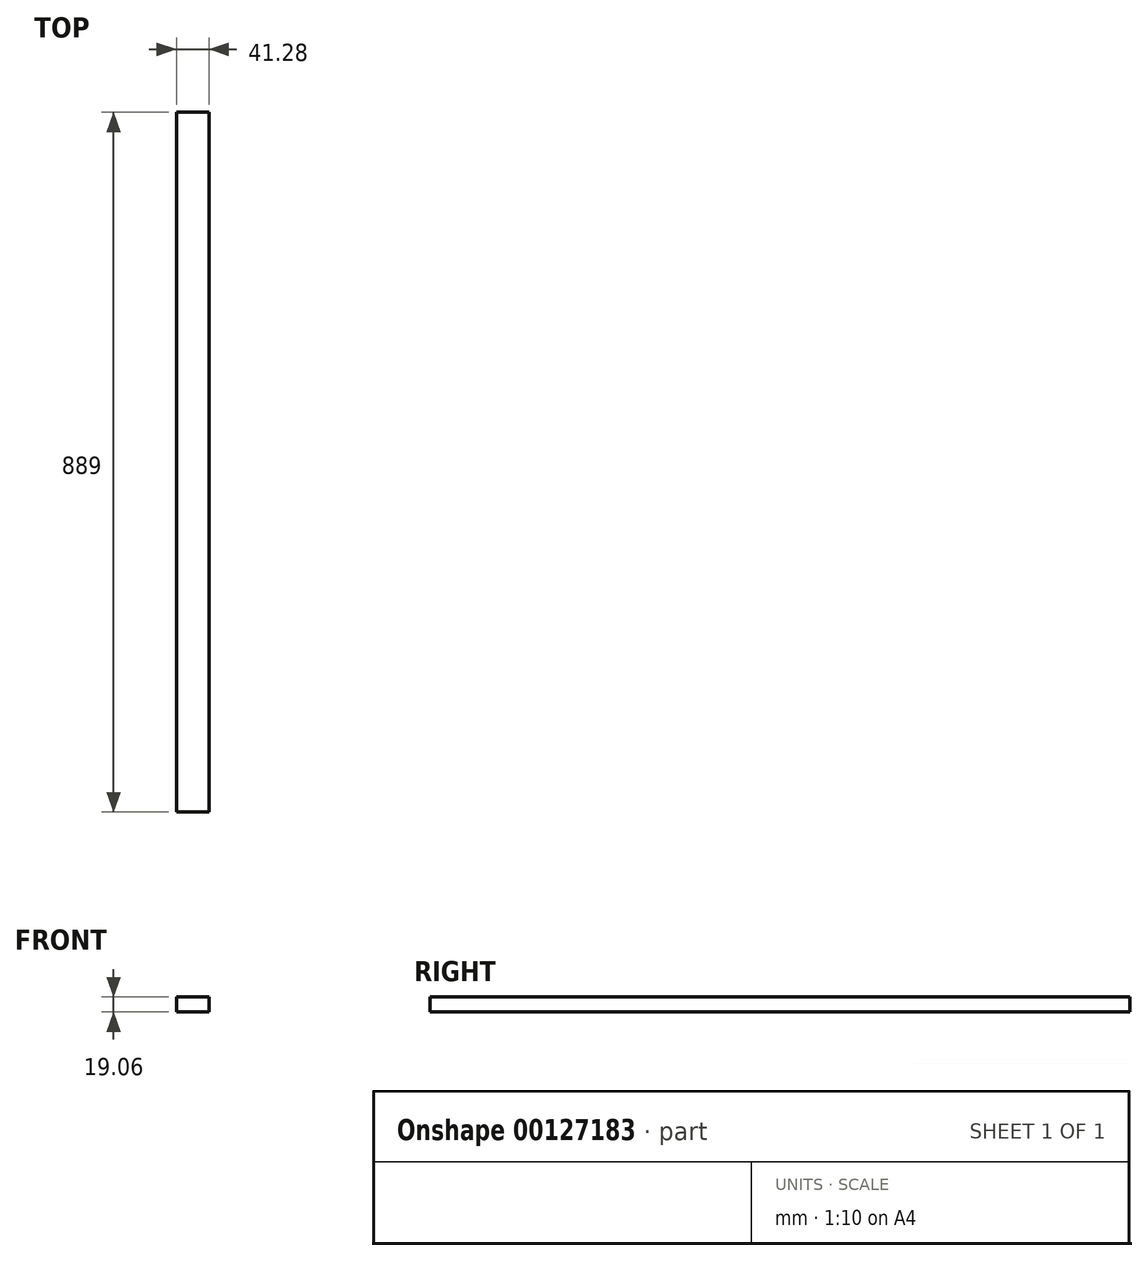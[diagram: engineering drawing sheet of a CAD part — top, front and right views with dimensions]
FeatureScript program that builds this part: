
annotation { "Feature Type Name" : "Feature", "Feature Type Description" : "" }
export const myFeature = defineFeature(function(context is Context, id is Id, definition is map)
    precondition{}
    {
        {
            var Q0;
            Q0=qCreatedBy(makeId("Front.planeOp"),FACE);
            var sketch = newSketch(context, id + "F0", { "sketchPlane" : qUnion([Q0])});
            skLineSegment(sketch, "E0.bottom", {"start": v(20.64, -9.52) * mm, "end": v(-20.64, -9.52) * mm});
            skLineSegment(sketch, "E0.top", {"start": v(20.64, 9.53) * mm, "end": v(-20.64, 9.53) * mm});
            skLineSegment(sketch, "E0.left", {"start": v(20.64, -9.52) * mm, "end": v(20.64, 9.53) * mm});
            skLineSegment(sketch, "E0.right", {"start": v(-20.64, -9.52) * mm, "end": v(-20.64, 9.53) * mm});
            skPoint(sketch, "E0.middle", {"position": v(0, 0) * mm});
            skSolve(sketch);
        }
        {
            var Q0;
            Q0=qSketchRegion(id+"F0",true);
            extrude(context, id + "F1", {"entities" : qUnion([Q0]), "depth" : 889 * mm});
        }
    });
